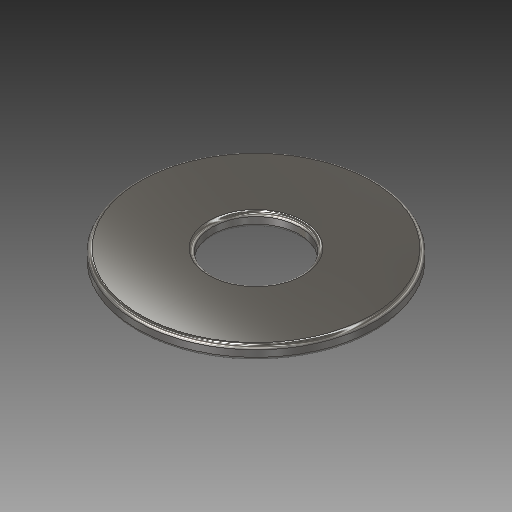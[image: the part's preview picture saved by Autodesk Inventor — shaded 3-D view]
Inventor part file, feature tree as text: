
AUTODESK INVENTOR PART (.ipt)
format: ipt  version: 2019.3 (Build 233278000, 278)  size: 143,872 bytes
history: native  units: mm
features: other x1, revolve x1, fillet x1, sketch x1
ambient origin geometry x8: Origin, YZ Plane, XZ Plane, XY Plane, X Axis, Y Axis, Z Axis, Center Point
bodies: Body1 (feature_tree)
feature tree (4):
  other  "Твердое тело1"
  revolve  "Вращение1"
  fillet  "Сопряжение3"  Radius=26.0mm
  sketch  "Эскиз1"
